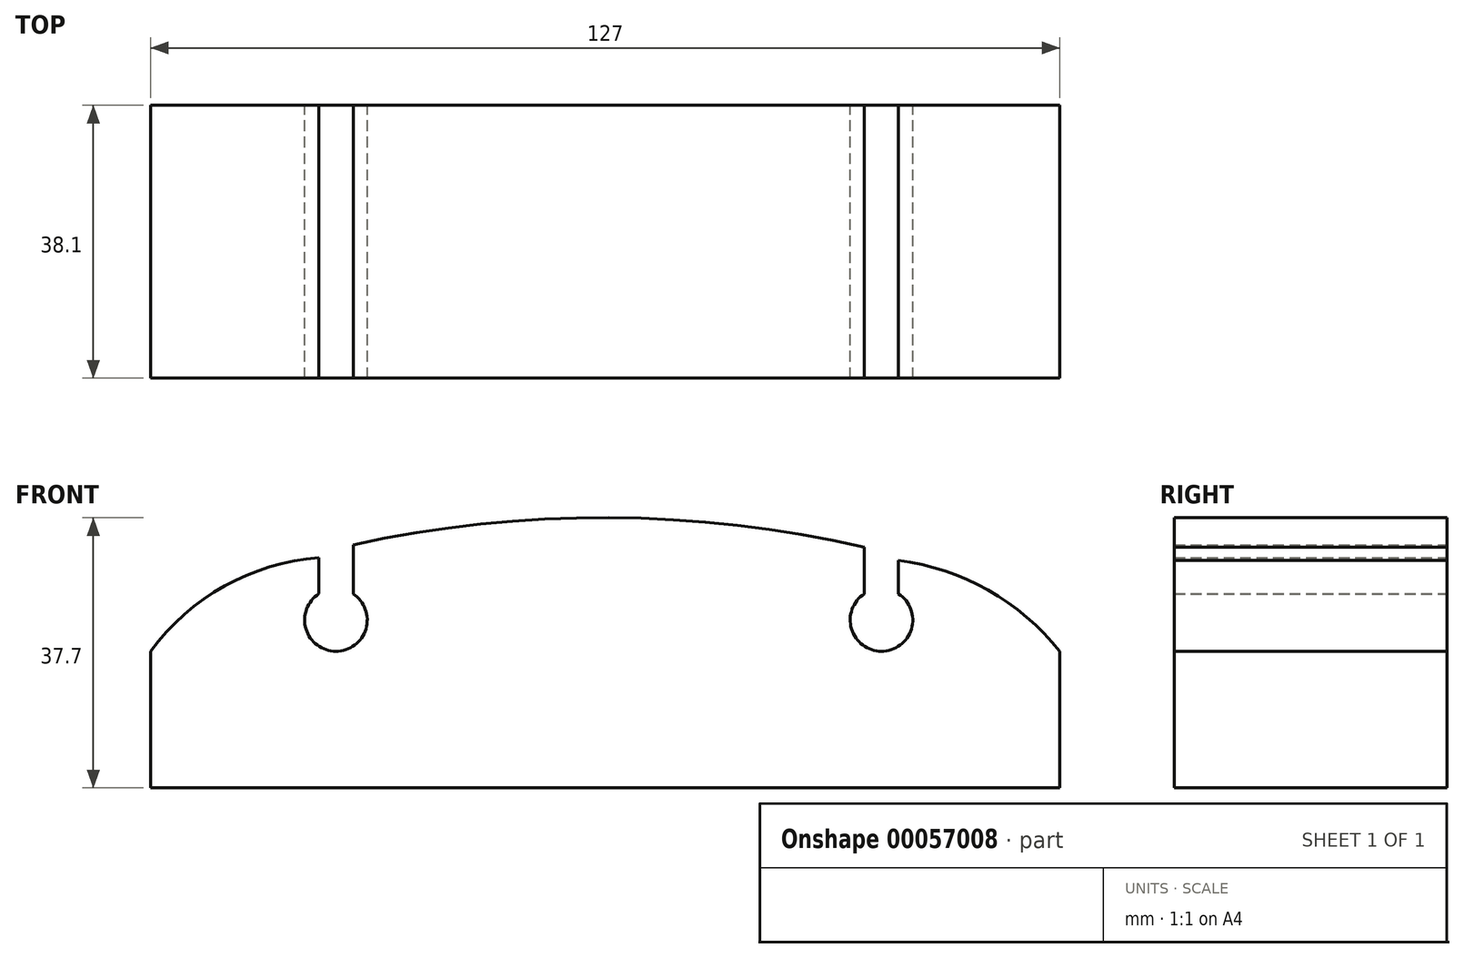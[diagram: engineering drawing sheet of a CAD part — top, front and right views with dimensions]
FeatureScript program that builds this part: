
annotation { "Feature Type Name" : "Feature", "Feature Type Description" : "" }
export const myFeature = defineFeature(function(context is Context, id is Id, definition is map)
    precondition{}
    {
        {
            var Q0;
            Q0=qCreatedBy(makeId("Front.planeOp"),FACE);
            var sketch = newSketch(context, id + "F0", { "sketchPlane" : qUnion([Q0])});
            skLineSegment(sketch, "E0", {"start": v(-64.9, 0) * mm, "end": v(62.1, 0) * mm});
            skLineSegment(sketch, "E1", {"start": v(-64.9, 0) * mm, "end": v(-64.9, 19.05) * mm});
            skLineSegment(sketch, "E2", {"start": v(62.1, 0) * mm, "end": v(62.1, 19.05) * mm});
            skArc(sketch, "E3", {"start": v(34.8, 27.08) * mm, "mid": v(37.19, 19.05) * mm, "end": v(39.57, 27.08) * mm});
            skLineSegment(sketch, "E4", {"start": v(34.8, 27.08) * mm, "end": v(34.8, 33.58) * mm});
            skLineSegment(sketch, "E5", {"start": v(39.57, 27.08) * mm, "end": v(39.57, 31.74) * mm});
            skArc(sketch, "E6", {"start": v(-41.4, 27.08) * mm, "mid": v(-39.03, 19.05) * mm, "end": v(-36.62, 27.07) * mm});
            skLineSegment(sketch, "E7", {"start": v(-36.62, 27.07) * mm, "end": v(-36.62, 33.93) * mm});
            skLineSegment(sketch, "E8", {"start": v(-41.4, 27.08) * mm, "end": v(-41.4, 32.14) * mm});
            skArc(sketch, "E9", {"start": v(62.1, 19.05) * mm, "mid": v(52.07, 27.6) * mm, "end": v(39.57, 31.74) * mm});
            skArc(sketch, "E10", {"start": v(-41.4, 32.14) * mm, "mid": v(-54.58, 28.17) * mm, "end": v(-64.9, 19.05) * mm});
            skArc(sketch, "E11", {"start": v(34.8, 33.58) * mm, "mid": v(-0.9, 37.7) * mm, "end": v(-36.62, 33.93) * mm});
            skSolve(sketch);
        }
        {
            var Q0;
            Q0 = qSketchRegion(id + "F0", true);
            extrude(context, id + "F1", {"entities" : qUnion([Q0]), "endBound" : BoundingType.SYMMETRIC, "depth" : 38.1 * mm});
        }
    });
